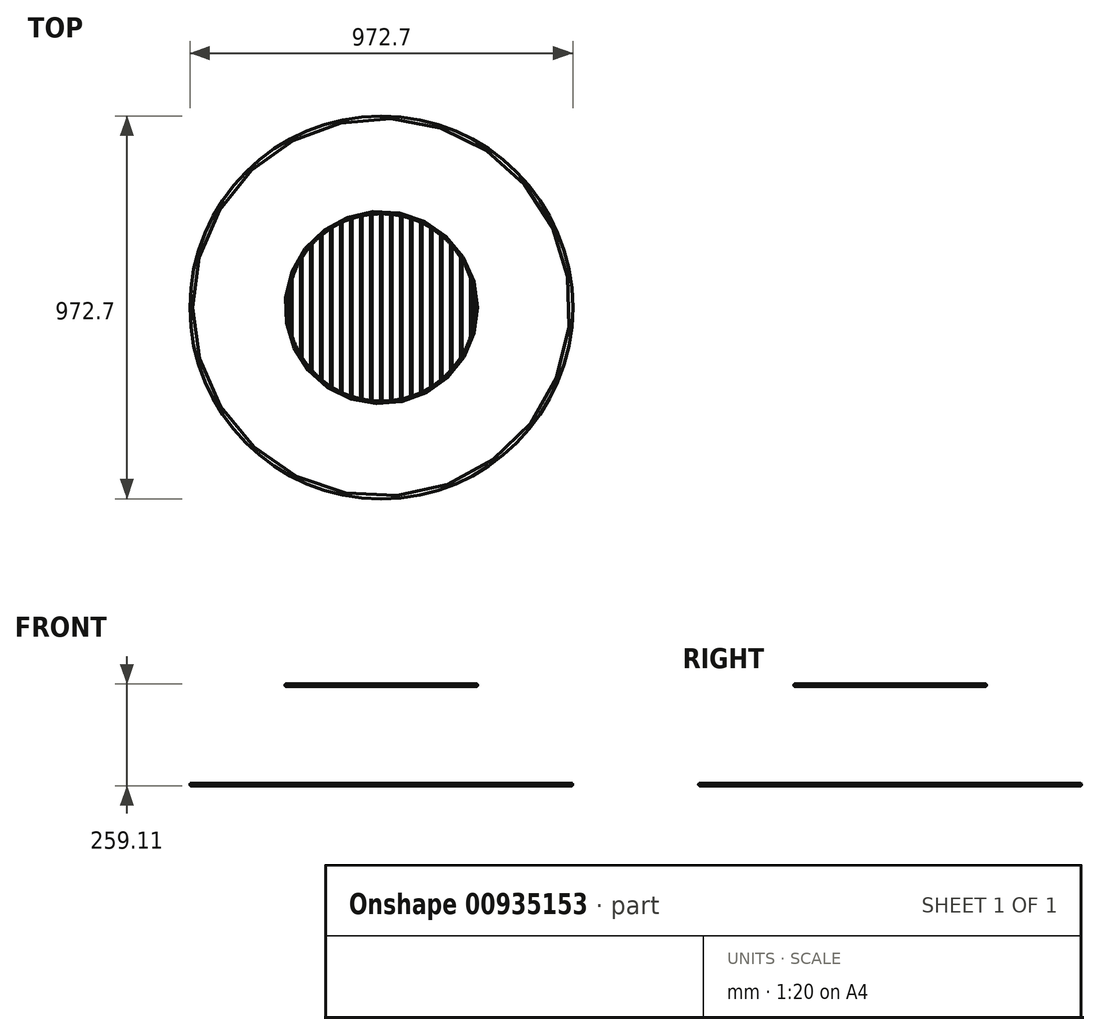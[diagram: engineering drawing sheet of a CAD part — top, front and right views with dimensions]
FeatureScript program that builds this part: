
annotation { "Feature Type Name" : "Feature", "Feature Type Description" : "" }
export const myFeature = defineFeature(function(context is Context, id is Id, definition is map)
    precondition{}
    {
        {
            var Q0;
            Q0=qCreatedBy(makeId("Front.planeOp"),FACE);
            var sketch = newSketch(context, id + "F0", { "sketchPlane" : qUnion([Q0])});
            skCircle(sketch, "E0", {"center": v(241.3, 0) * mm, "radius": 3.18 * mm});
            skLineSegment(sketch, "E1", {"start": v(0, 0) * mm, "end": v(0, 32.12) * mm, "construction": true});
            skCircle(sketch, "E2", {"center": v(483.15, -252.73) * mm, "radius": 3.2 * mm});
            skLineSegment(sketch, "E3", {"start": v(0, -252.73) * mm, "end": v(0, 0) * mm});
            skSolve(sketch);
        }
        {
            var Q0;
            Q0=makeQuery(id+"F0.imprint","IMPRINT",FACE,{"disambiguationData":[TD([[makeQuery(id+"F0.imprint","IMPRINT",EDGE,{"derivedFrom":sQuery(id+"F0.wireOp",EDGE,"E0")}),1.0]])]});
            var Q1;
            Q1=sQuery(id+"F0.wireOp",EDGE,"E1");
            revolve(context, id + "F1", {"entities" : qUnion([Q0]), "axis" : qUnion([Q1]), "revolveType" : RevolveType.FULL});
        }
        {
            var Q0;
            Q0=qCreatedBy(makeId("Front.planeOp"),FACE);
            var sketch = newSketch(context, id + "F2", { "sketchPlane" : qUnion([Q0])});
            skCircle(sketch, "E4", {"center": v(0, 0) * mm, "radius": 1.59 * mm});
            skCircle(sketch, "E5.1.0.0", {"center": v(25.4, 0) * mm, "radius": 1.59 * mm});
            skCircle(sketch, "E5.2.0.0", {"center": v(50.8, 0) * mm, "radius": 1.59 * mm});
            skCircle(sketch, "E5.3.0.0", {"center": v(76.2, 0) * mm, "radius": 1.59 * mm});
            skCircle(sketch, "E5.4.0.0", {"center": v(101.6, 0) * mm, "radius": 1.59 * mm});
            skCircle(sketch, "E5.5.0.0", {"center": v(127, 0) * mm, "radius": 1.59 * mm});
            skCircle(sketch, "E5.6.0.0", {"center": v(152.4, 0) * mm, "radius": 1.59 * mm});
            skCircle(sketch, "E5.7.0.0", {"center": v(177.8, 0) * mm, "radius": 1.59 * mm});
            skCircle(sketch, "E5.8.0.0", {"center": v(203.2, 0) * mm, "radius": 1.59 * mm});
            skCircle(sketch, "E5.9.0.0", {"center": v(228.6, 0) * mm, "radius": 1.59 * mm});
            skLineSegment(sketch, "E5.direction1", {"start": v(0, 0) * mm, "end": v(25.4, 0) * mm, "construction": true});
            skCircle(sketch, "E6.1.0.0", {"center": v(-25.4, 0) * mm, "radius": 1.59 * mm});
            skCircle(sketch, "E6.2.0.0", {"center": v(-50.8, 0) * mm, "radius": 1.59 * mm});
            skCircle(sketch, "E6.3.0.0", {"center": v(-76.2, 0) * mm, "radius": 1.59 * mm});
            skCircle(sketch, "E6.4.0.0", {"center": v(-101.6, 0) * mm, "radius": 1.59 * mm});
            skCircle(sketch, "E6.5.0.0", {"center": v(-127, 0) * mm, "radius": 1.59 * mm});
            skCircle(sketch, "E6.6.0.0", {"center": v(-152.4, 0) * mm, "radius": 1.59 * mm});
            skCircle(sketch, "E6.7.0.0", {"center": v(-177.8, 0) * mm, "radius": 1.59 * mm});
            skCircle(sketch, "E6.8.0.0", {"center": v(-203.2, 0) * mm, "radius": 1.59 * mm});
            skCircle(sketch, "E6.9.0.0", {"center": v(-228.6, 0) * mm, "radius": 1.59 * mm});
            skLineSegment(sketch, "E6.direction1", {"start": v(0, 0) * mm, "end": v(-25.4, 0) * mm, "construction": true});
            skSolve(sketch);
        }
        {
            var Q0;
            Q0=qSketchRegion(id+"F2",true);
            extrude(context, id + "F3", {"entities" : qUnion([Q0]), "operationType" : NewBodyOperationType.ADD, "endBound" : BoundingType.UP_TO_NEXT, "depth" : 25.4 * mm, "hasSecondDirection" : true, "secondDirectionBound" : SecondDirectionBoundingType.UP_TO_NEXT, "secondDirectionOppositeDirection" : true, "secondDirectionDepth" : 25.4 * mm});
        }
        {
            var Q0;
            Q0=makeQuery(id+"F0.imprint","IMPRINT",FACE,{"disambiguationData":[TD([[makeQuery(id+"F0.imprint","IMPRINT",EDGE,{"derivedFrom":sQuery(id+"F0.wireOp",EDGE,"E2")}),1.0]])]});
            var Q1;
            Q1=sQuery(id+"F0.wireOp",EDGE,"E3");
            revolve(context, id + "F4", {"surfaceOperationType" : NewSurfaceOperationType.NEW, "entities" : qUnion([Q0]), "axis" : qUnion([Q1]), "revolveType" : RevolveType.FULL});
        }
    });
